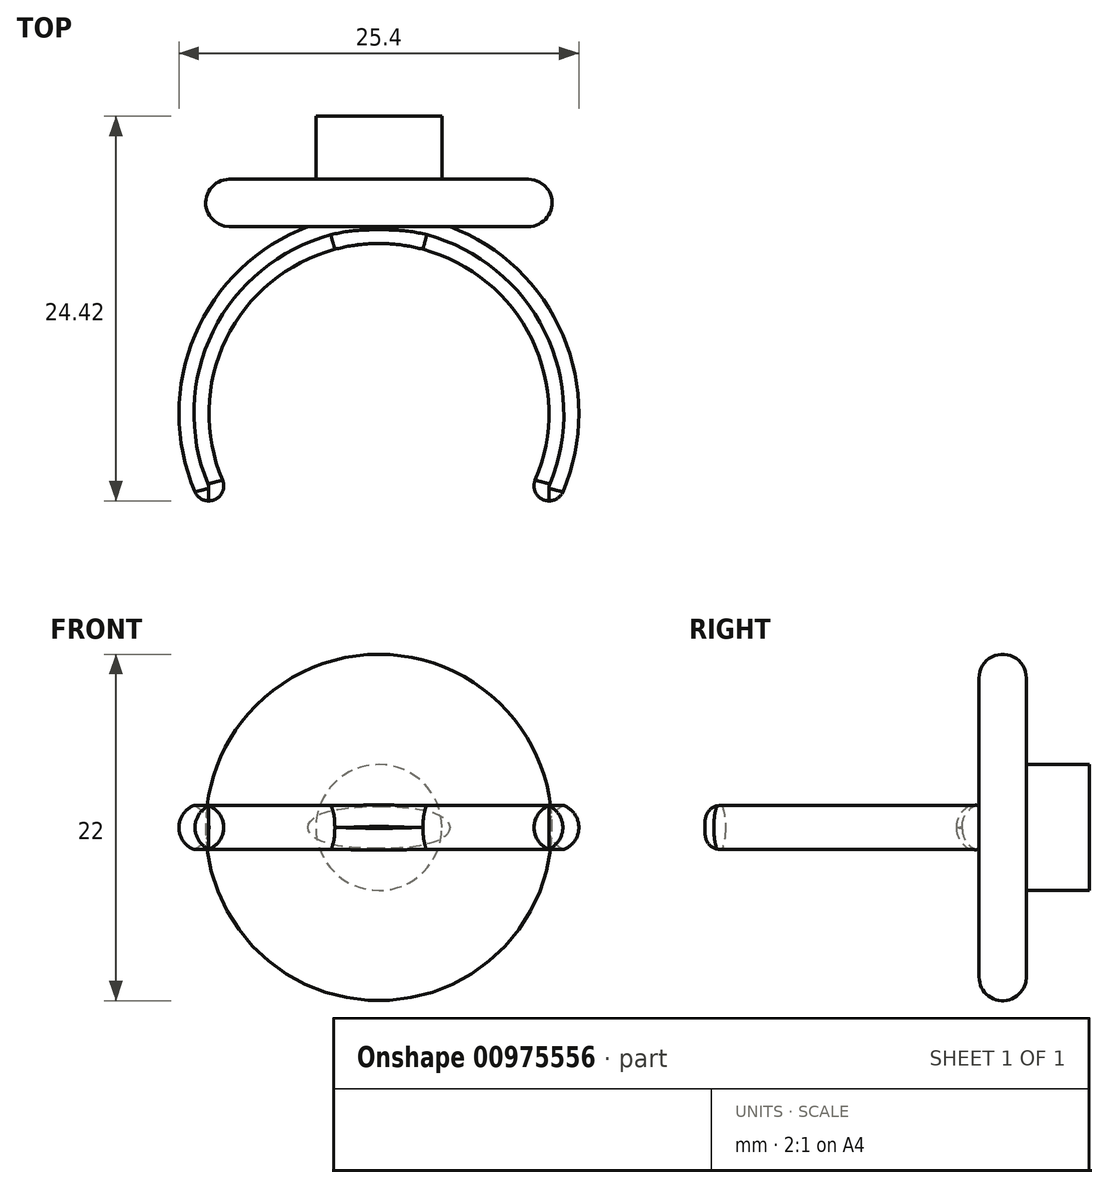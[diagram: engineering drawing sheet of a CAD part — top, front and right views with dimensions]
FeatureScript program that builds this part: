
annotation { "Feature Type Name" : "Feature", "Feature Type Description" : "" }
export const myFeature = defineFeature(function(context is Context, id is Id, definition is map)
    precondition{}
    {
        {
            var Q0;
            Q0=qCreatedBy(makeId("Top.planeOp"),FACE);
            var sketch = newSketch(context, id + "F0", { "sketchPlane" : qUnion([Q0])});
            skArc(sketch, "E0", {"start": v(9.26, -5.55) * mm, "mid": v(0, 10.8) * mm, "end": v(-9.26, -5.55) * mm});
            skArc(sketch, "E1", {"start": v(11.42, -5.55) * mm, "mid": v(11.8, 4.69) * mm, "end": v(4.5, 11.87) * mm});
            skPoint(sketch, "E2", {"position": v(0, 12.7) * mm});
            skLineSegment(sketch, "E3.bottom", {"start": v(4.5, 11.87) * mm, "end": v(-4.5, 11.87) * mm});
            skLineSegment(sketch, "E4", {"start": v(0, 0) * mm, "end": v(0, 9.7) * mm});
            skLineSegment(sketch, "E5", {"start": v(-9.26, -5.55) * mm, "end": v(-11.42, -5.55) * mm});
            skLineSegment(sketch, "E6.MirrorCS", {"start": v(9.26, -5.55) * mm, "end": v(11.42, -5.55) * mm});
            skArc(sketch, "E7.trimOffspring", {"start": v(-4.5, 11.87) * mm, "mid": v(-11.8, 4.69) * mm, "end": v(-11.42, -5.55) * mm});
            skPoint(sketch, "E3.left.end.orphan", {"position": v(4.5, 13.53) * mm});
            skPoint(sketch, "E3.right.end.orphan", {"position": v(-4.5, 13.53) * mm});
            skSolve(sketch);
        }
        {
            var Q0;
            Q0=makeQuery(id+"F0.imprint","IMPRINT",FACE,{"disambiguationData":[TD([[makeQuery(id+"F0.imprint","IMPRINT",EDGE,{"derivedFrom":sQuery(id+"F0.wireOp",EDGE,"E0")}),-1.0]])]});
            extrude(context, id + "F1", {"entities" : qUnion([Q0]), "depth" : 3 * mm, "offsetDistance" : 25.4 * mm});
        }
        {
            var Q0;
            Q0=makeQuery(id+"F1.opExtrude","SWEPT_FACE",FACE,{"disambiguationData":[OSD([sQuery(id+"F0.wireOp",EDGE,"E3.bottom")])]});
            var sketch = newSketch(context, id + "F2", { "sketchPlane" : qUnion([Q0])});
            skCircle(sketch, "E8", {"center": v(0, 1.5) * mm, "radius": 11 * mm});
            skPoint(sketch, "E8.centerSnap0", {"position": v(4.5, 1.5) * mm});
            skPoint(sketch, "E8.centerSnap1", {"position": v(0, 0) * mm});
            skSolve(sketch);
        }
        {
            var Q0;
            Q0 = qSketchRegion(id + "F2", true);
            extrude(context, id + "F3", {"entities" : qUnion([Q0]), "operationType" : NewBodyOperationType.ADD, "depth" : 3 * mm, "offsetDistance" : 25.4 * mm});
        }
        {
            var Q0;
            Q0=makeQuery(id+"F3.opExtrude","CAP_FACE",FACE,{"disambiguationData":[OSD([sQuery(id+"F2.wireOp",EDGE,"E8")])],"isStart":false});
            var sketch = newSketch(context, id + "F4", { "sketchPlane" : qUnion([Q0])});
            skPoint(sketch, "E9", {"position": v(0, 1.5) * mm});
            skCircle(sketch, "E10", {"center": v(0, 1.5) * mm, "radius": 4 * mm});
            skSolve(sketch);
        }
        {
            var Q0;
            Q0 = qSketchRegion(id + "F4", true);
            extrude(context, id + "F5", {"entities" : qUnion([Q0]), "operationType" : NewBodyOperationType.ADD, "depth" : 4 * mm, "offsetDistance" : 25.4 * mm});
        }
        {
            var Q0;
            Q0=makeQuery(id+"F1.opExtrude","CAP_EDGE",EDGE,{"disambiguationData":[OSD([sQuery(id+"F0.wireOp",EDGE,"E0")])],"isStart":true});
            var Q1;
            Q1=makeQuery(id+"F1.opExtrude","CAP_EDGE",EDGE,{"disambiguationData":[OSD([sQuery(id+"F0.wireOp",EDGE,"E7.trimOffspring")])],"isStart":false});
            var Q2;
            Q2=makeQuery(id+"F1.opExtrude","CAP_EDGE",EDGE,{"disambiguationData":[OSD([sQuery(id+"F0.wireOp",EDGE,"E7.trimOffspring")])],"isStart":true});
            var Q3;
            Q3=makeQuery(id+"F1.opExtrude","CAP_EDGE",EDGE,{"disambiguationData":[OSD([sQuery(id+"F0.wireOp",EDGE,"E1")])],"isStart":false});
            var Q4;
            Q4=makeQuery(id+"F1.opExtrude","CAP_EDGE",EDGE,{"disambiguationData":[OSD([sQuery(id+"F0.wireOp",EDGE,"E0")])],"isStart":false});
            var Q5;
            Q5=makeQuery(id+"F1.opExtrude","CAP_EDGE",EDGE,{"disambiguationData":[OSD([sQuery(id+"F0.wireOp",EDGE,"E1")])],"isStart":true});
            fillet(context, id + "F6", {"entities" : qUnion([Q0, Q1, Q2, Q3, Q4, Q5]), "radius" : 1.5 * mm, "tangentPropagation" : true, "allowEdgeOverflow" : false});
        }
        {
            var Q0;
            Q0=makeQuery(id+"F6.opFillet","BLEND_EDGE",EDGE,{"blendedFrom":[makeQuery(id+"F1.opExtrude","CAP_EDGE",EDGE,{"disambiguationData":[OSD([sQuery(id+"F0.wireOp",EDGE,"E1")])],"isStart":true}),makeQuery(id+"F1.opExtrude","SWEPT_FACE",FACE,{"disambiguationData":[OSD([sQuery(id+"F0.wireOp",EDGE,"E6.MirrorCS")])]})],"blendedInto":[makeQuery(id+"F1.opExtrude","SWEPT_FACE",FACE,{"disambiguationData":[OSD([sQuery(id+"F0.wireOp",EDGE,"E6.MirrorCS")])]})]});
            var Q1;
            Q1=makeQuery(id+"F6.opFillet","BLEND_EDGE",EDGE,{"blendedFrom":[makeQuery(id+"F1.opExtrude","CAP_EDGE",EDGE,{"disambiguationData":[OSD([sQuery(id+"F0.wireOp",EDGE,"E0")])],"isStart":false}),makeQuery(id+"F1.opExtrude","SWEPT_FACE",FACE,{"disambiguationData":[OSD([sQuery(id+"F0.wireOp",EDGE,"E6.MirrorCS")])]})],"blendedInto":[makeQuery(id+"F1.opExtrude","SWEPT_FACE",FACE,{"disambiguationData":[OSD([sQuery(id+"F0.wireOp",EDGE,"E6.MirrorCS")])]})]});
            var Q2;
            Q2=makeQuery(id+"F6.opFillet","BLEND_EDGE",EDGE,{"blendedFrom":[makeQuery(id+"F1.opExtrude","CAP_EDGE",EDGE,{"disambiguationData":[OSD([sQuery(id+"F0.wireOp",EDGE,"E0")])],"isStart":true}),makeQuery(id+"F1.opExtrude","SWEPT_FACE",FACE,{"disambiguationData":[OSD([sQuery(id+"F0.wireOp",EDGE,"E6.MirrorCS")])]})],"blendedInto":[makeQuery(id+"F1.opExtrude","SWEPT_FACE",FACE,{"disambiguationData":[OSD([sQuery(id+"F0.wireOp",EDGE,"E6.MirrorCS")])]})]});
            var Q3;
            Q3=makeQuery(id+"F6.opFillet","BLEND_EDGE",EDGE,{"blendedFrom":[makeQuery(id+"F1.opExtrude","CAP_EDGE",EDGE,{"disambiguationData":[OSD([sQuery(id+"F0.wireOp",EDGE,"E1")])],"isStart":false}),makeQuery(id+"F1.opExtrude","SWEPT_FACE",FACE,{"disambiguationData":[OSD([sQuery(id+"F0.wireOp",EDGE,"E6.MirrorCS")])]})],"blendedInto":[makeQuery(id+"F1.opExtrude","SWEPT_FACE",FACE,{"disambiguationData":[OSD([sQuery(id+"F0.wireOp",EDGE,"E6.MirrorCS")])]})]});
            var Q4;
            Q4=makeQuery(id+"F6.opFillet","BLEND_EDGE",EDGE,{"blendedFrom":[makeQuery(id+"F1.opExtrude","CAP_EDGE",EDGE,{"disambiguationData":[OSD([sQuery(id+"F0.wireOp",EDGE,"E7.trimOffspring")])],"isStart":false}),makeQuery(id+"F1.opExtrude","SWEPT_FACE",FACE,{"disambiguationData":[OSD([sQuery(id+"F0.wireOp",EDGE,"E5")])]})],"blendedInto":[makeQuery(id+"F1.opExtrude","SWEPT_FACE",FACE,{"disambiguationData":[OSD([sQuery(id+"F0.wireOp",EDGE,"E5")])]})]});
            var Q5;
            Q5=makeQuery(id+"F6.opFillet","BLEND_EDGE",EDGE,{"blendedFrom":[makeQuery(id+"F1.opExtrude","CAP_EDGE",EDGE,{"disambiguationData":[OSD([sQuery(id+"F0.wireOp",EDGE,"E7.trimOffspring")])],"isStart":true}),makeQuery(id+"F1.opExtrude","SWEPT_FACE",FACE,{"disambiguationData":[OSD([sQuery(id+"F0.wireOp",EDGE,"E5")])]})],"blendedInto":[makeQuery(id+"F1.opExtrude","SWEPT_FACE",FACE,{"disambiguationData":[OSD([sQuery(id+"F0.wireOp",EDGE,"E5")])]})]});
            var Q6;
            Q6=makeQuery(id+"F6.opFillet","BLEND_EDGE",EDGE,{"blendedFrom":[makeQuery(id+"F1.opExtrude","CAP_EDGE",EDGE,{"disambiguationData":[OSD([sQuery(id+"F0.wireOp",EDGE,"E0")])],"isStart":false}),makeQuery(id+"F1.opExtrude","SWEPT_FACE",FACE,{"disambiguationData":[OSD([sQuery(id+"F0.wireOp",EDGE,"E5")])]})],"blendedInto":[makeQuery(id+"F1.opExtrude","SWEPT_FACE",FACE,{"disambiguationData":[OSD([sQuery(id+"F0.wireOp",EDGE,"E5")])]})]});
            var Q7;
            Q7=makeQuery(id+"F6.opFillet","BLEND_EDGE",EDGE,{"blendedFrom":[makeQuery(id+"F1.opExtrude","CAP_EDGE",EDGE,{"disambiguationData":[OSD([sQuery(id+"F0.wireOp",EDGE,"E0")])],"isStart":true}),makeQuery(id+"F1.opExtrude","SWEPT_FACE",FACE,{"disambiguationData":[OSD([sQuery(id+"F0.wireOp",EDGE,"E5")])]})],"blendedInto":[makeQuery(id+"F1.opExtrude","SWEPT_FACE",FACE,{"disambiguationData":[OSD([sQuery(id+"F0.wireOp",EDGE,"E5")])]})]});
            fillet(context, id + "F7", {"entities" : qUnion([Q0, Q1, Q2, Q3, Q4, Q5, Q6, Q7]), "radius" : 0.94 * mm, "tangentPropagation" : true, "allowEdgeOverflow" : false});
        }
        {
            var Q0;
            Q0=makeQuery(id+"F3.opExtrude","CAP_EDGE",EDGE,{"disambiguationData":[OSD([sQuery(id+"F2.wireOp",EDGE,"E8")])],"isStart":true});
            var Q1;
            Q1=makeQuery(id+"F3.opExtrude","CAP_EDGE",EDGE,{"disambiguationData":[OSD([sQuery(id+"F2.wireOp",EDGE,"E8")])],"isStart":false});
            var Q2;
            Q2=makeQuery(id+"F5.opExtrude","CAP_EDGE",EDGE,{"disambiguationData":[OSD([sQuery(id+"F4.wireOp",EDGE,"E10")])],"isStart":true});
            fillet(context, id + "F8", {"entities" : qUnion([Q0, Q1, Q2]), "radius" : 1.5 * mm, "tangentPropagation" : true, "allowEdgeOverflow" : false});
        }
    });
